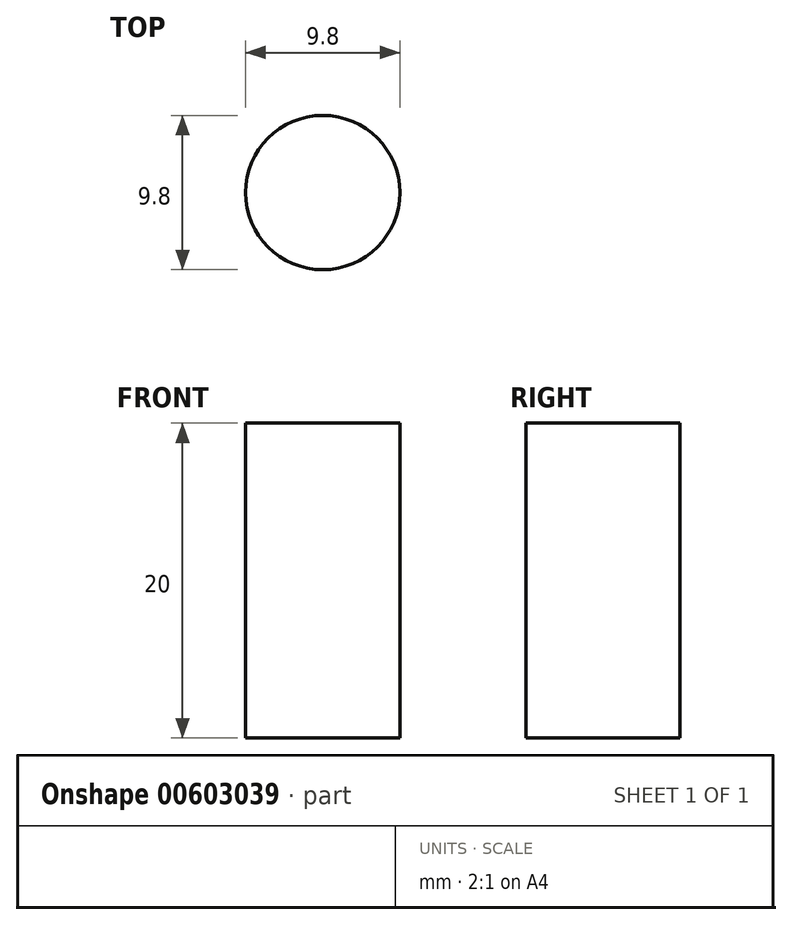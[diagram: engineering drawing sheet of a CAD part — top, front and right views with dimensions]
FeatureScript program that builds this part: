
annotation { "Feature Type Name" : "Feature", "Feature Type Description" : "" }
export const myFeature = defineFeature(function(context is Context, id is Id, definition is map)
    precondition{}
    {
        {
            var Q0;
            Q0=qCreatedBy(makeId("Top.planeOp"),FACE);
            var sketch = newSketch(context, id + "F0", { "sketchPlane" : qUnion([Q0])});
            skCircle(sketch, "E0", {"center": v(0, 0) * mm, "radius": 4.9 * mm});
            skSolve(sketch);
        }
        {
            var Q0;
            Q0 = qSketchRegion(id + "F0", true);
            extrude(context, id + "F1", {"entities" : qUnion([Q0]), "depth" : 20 * mm, "offsetDistance" : 25 * mm});
        }
    });
